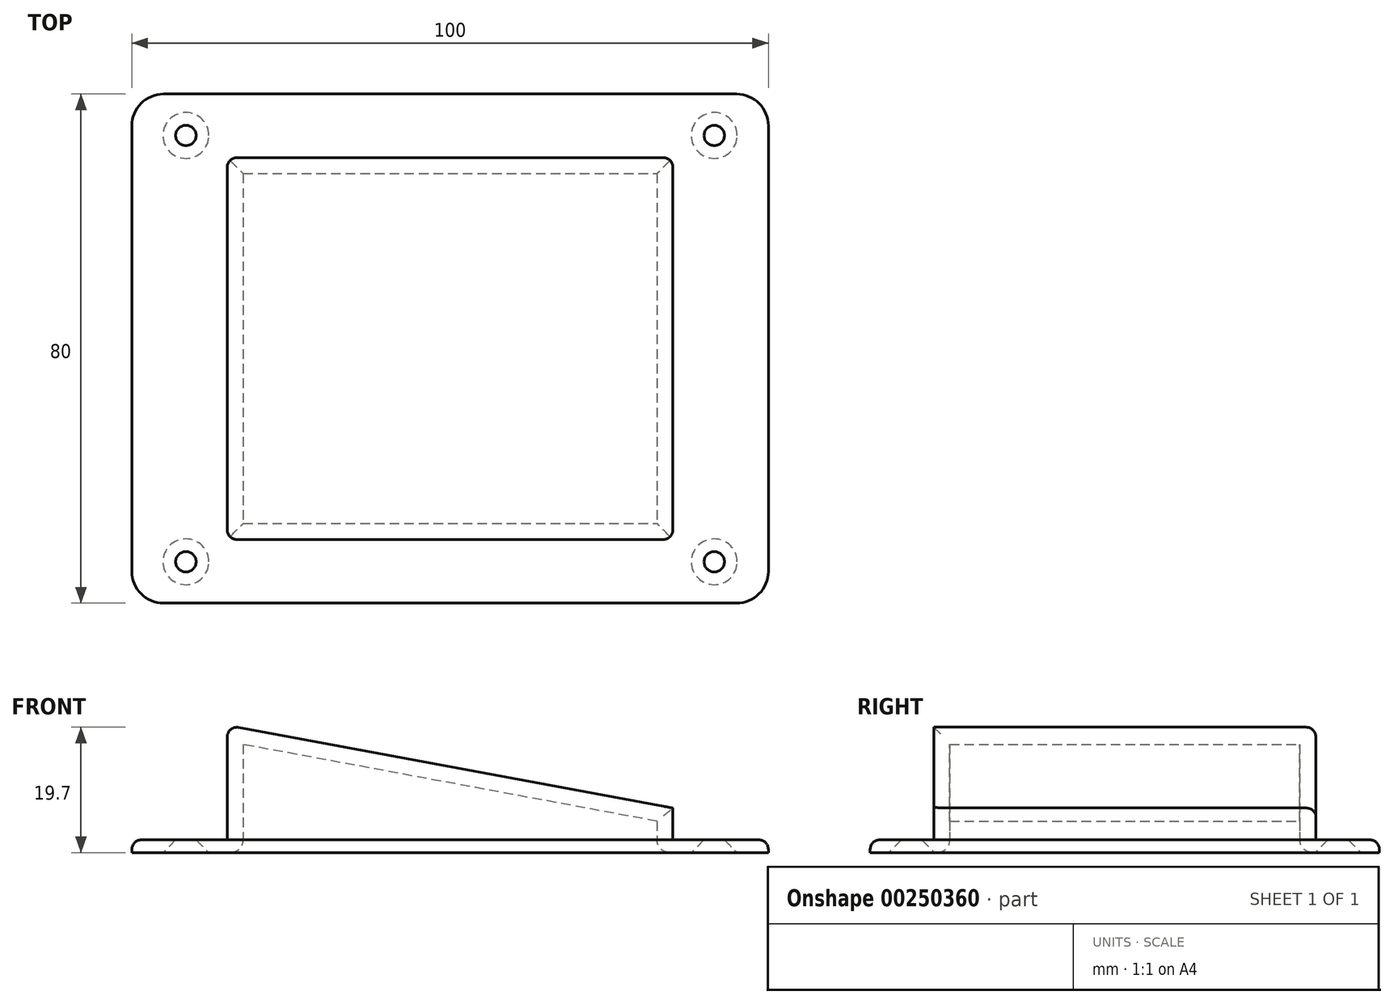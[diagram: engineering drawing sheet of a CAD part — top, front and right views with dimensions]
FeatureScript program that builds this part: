
annotation { "Feature Type Name" : "Feature", "Feature Type Description" : "" }
export const myFeature = defineFeature(function(context is Context, id is Id, definition is map)
    precondition{}
    {
        {
            var Q0;
            Q0=qCreatedBy(makeId("Top.planeOp"),FACE);
            var sketch = newSketch(context, id + "F0", { "sketchPlane" : qUnion([Q0])});
            skLineSegment(sketch, "E0.bottom", {"start": v(50, -40) * mm, "end": v(-50, -40) * mm});
            skLineSegment(sketch, "E0.top", {"start": v(50, 40) * mm, "end": v(-50, 40) * mm});
            skLineSegment(sketch, "E0.left", {"start": v(50, -40) * mm, "end": v(50, 40) * mm});
            skLineSegment(sketch, "E0.right", {"start": v(-50, -40) * mm, "end": v(-50, 40) * mm});
            skPoint(sketch, "E0.middle", {"position": v(0, 0) * mm});
            skSolve(sketch);
        }
        {
            var Q0;
            Q0=qSketchRegion(id+"F0",true);
            extrude(context, id + "F1", {"entities" : qUnion([Q0]), "depth" : 2 * mm});
        }
        {
            var Q0;
            Q0=makeQuery(id+"F1.opExtrude","CAP_FACE",FACE,{"disambiguationData":[OSD([sQuery(id+"F0.wireOp",EDGE,"E0.bottom"),sQuery(id+"F0.wireOp",EDGE,"E0.top"),sQuery(id+"F0.wireOp",EDGE,"E0.left"),sQuery(id+"F0.wireOp",EDGE,"E0.right")])],"isStart":false});
            var sketch = newSketch(context, id + "F2", { "sketchPlane" : qUnion([Q0])});
            skLineSegment(sketch, "E1.bottom", {"start": v(35, -30) * mm, "end": v(-35, -30) * mm});
            skLineSegment(sketch, "E1.top", {"start": v(35, 30) * mm, "end": v(-35, 30) * mm});
            skLineSegment(sketch, "E1.left", {"start": v(35, -30) * mm, "end": v(35, 30) * mm});
            skLineSegment(sketch, "E1.right", {"start": v(-35, -30) * mm, "end": v(-35, 30) * mm});
            skPoint(sketch, "E1.middle", {"position": v(0, 0) * mm});
            skSolve(sketch);
        }
        {
            var Q0;
            Q0=qSketchRegion(id+"F2",true);
            extrude(context, id + "F3", {"entities" : qUnion([Q0]), "operationType" : NewBodyOperationType.ADD, "depth" : 18 * mm});
        }
        {
            var Q0;
            Q0=makeQuery(id+"F3.opExtrude","CAP_FACE",FACE,{"disambiguationData":[OSD([sQuery(id+"F2.wireOp",EDGE,"E1.bottom"),sQuery(id+"F2.wireOp",EDGE,"E1.top"),sQuery(id+"F2.wireOp",EDGE,"E1.left"),sQuery(id+"F2.wireOp",EDGE,"E1.right")])],"isStart":false});
            shell(context, id + "F4", {"entities" : qUnion([Q0]), "thickness" : 2.5 * mm});
        }
        {
            var Q0;
            Q0=makeQuery(id+"F3.opExtrude","SWEPT_FACE",FACE,{"disambiguationData":[OSD([sQuery(id+"F2.wireOp",EDGE,"E1.bottom")])]});
            var sketch = newSketch(context, id + "F5", { "sketchPlane" : qUnion([Q0])});
            skLineSegment(sketch, "E2", {"start": v(-31.99, 7) * mm, "end": v(36.9, 7) * mm});
            skLineSegment(sketch, "E3", {"start": v(-35, 20) * mm, "end": v(35, 7) * mm});
            skLineSegment(sketch, "E4", {"start": v(35, 7) * mm, "end": v(35, 20) * mm});
            skLineSegment(sketch, "E5", {"start": v(35, 20) * mm, "end": v(-35, 20) * mm});
            skSolve(sketch);
        }
        {
            var Q0;
            Q0=qSketchRegion(id+"F5",true);
            extrude(context, id + "F6", {"entities" : qUnion([Q0]), "operationType" : NewBodyOperationType.REMOVE, "oppositeDirection" : true, "depth" : 120 * mm});
        }
        {
            var Q0;
            Q0=makeQuery(id+"F4.opShell","OFFSET_FACE",FACE,{"disambiguationData":[OSD([sQuery(id+"F0.wireOp",EDGE,"E0.bottom"),sQuery(id+"F0.wireOp",EDGE,"E0.top"),sQuery(id+"F0.wireOp",EDGE,"E0.left"),sQuery(id+"F0.wireOp",EDGE,"E0.right")])]});
            extrude(context, id + "F7", {"entities" : qUnion([Q0]), "operationType" : NewBodyOperationType.REMOVE, "oppositeDirection" : true, "depth" : 10 * mm});
        }
        {
            var Q0;
            Q0=makeQuery(id+"F6.boolean.opBoolean","COPY",FACE,{"derivedFrom":makeQuery(id+"F6.opExtrude","SWEPT_FACE",FACE,{"disambiguationData":[OSD([sQuery(id+"F5.wireOp",EDGE,"E3")])]})});
            var sketch = newSketch(context, id + "F8", { "sketchPlane" : qUnion([Q0])});
            skLineSegment(sketch, "E6.bottom", {"start": v(33.13, -30) * mm, "end": v(-37.75, -30) * mm});
            skLineSegment(sketch, "E6.top", {"start": v(33.13, 30) * mm, "end": v(-37.75, 30) * mm});
            skLineSegment(sketch, "E6.left", {"start": v(33.13, -30) * mm, "end": v(33.13, 30) * mm});
            skLineSegment(sketch, "E6.right", {"start": v(-37.75, -30) * mm, "end": v(-37.75, 30) * mm});
            skPoint(sketch, "E6.middle", {"position": v(-2.31, 0) * mm});
            skSolve(sketch);
        }
        {
            var Q0;
            Q0=makeQuery(id+"F8.imprint","IMPRINT",FACE,{"disambiguationData":[TD([[makeQuery(id+"F8.imprint","IMPRINT",EDGE,{"derivedFrom":sQuery(id+"F8.wireOp",EDGE,"E6.bottom")}),1.0]])]});
            var sketch = newSketch(context, id + "F9", { "sketchPlane" : qUnion([Q0])});
            skLineSegment(sketch, "E7.bottom", {"start": v(33.06, -29.96) * mm, "end": v(-38, -29.96) * mm});
            skLineSegment(sketch, "E7.top", {"start": v(33.06, 29.96) * mm, "end": v(-38, 29.96) * mm});
            skLineSegment(sketch, "E7.left", {"start": v(33.06, -29.96) * mm, "end": v(33.06, 29.96) * mm});
            skLineSegment(sketch, "E7.right", {"start": v(-38, -29.96) * mm, "end": v(-38, 29.96) * mm});
            skPoint(sketch, "E7.middle", {"position": v(-2.48, 0) * mm});
            skSolve(sketch);
        }
        {
            var Q0;
            Q0=qSketchRegion(id+"F9",true);
            extrude(context, id + "F10", {"entities" : qUnion([Q0]), "operationType" : NewBodyOperationType.ADD, "oppositeDirection" : true, "depth" : 2.5 * mm});
        }
        {
            var Q0;
            Q0=makeQuery(id+"F10.opExtrude","SWEPT_FACE",FACE,{"disambiguationData":[OSD([sQuery(id+"F9.wireOp",EDGE,"E7.bottom")])]});
            var sketch = newSketch(context, id + "F11", { "sketchPlane" : qUnion([Q0])});
            skLineSegment(sketch, "E8", {"start": v(-35, 19.7) * mm, "end": v(-35.4, 17.53) * mm});
            skLineSegment(sketch, "E9", {"start": v(-35.4, 17.53) * mm, "end": v(-35, 17.46) * mm});
            skLineSegment(sketch, "E10", {"start": v(-35, 17.46) * mm, "end": v(-35, 19.7) * mm});
            skSolve(sketch);
        }
        {
            var Q0;
            Q0=makeQuery(id+"F11.imprint","IMPRINT",FACE,{"disambiguationData":[TD([[makeQuery(id+"F11.imprint","IMPRINT",EDGE,{"derivedFrom":sQuery(id+"F11.wireOp",EDGE,"E8")}),-1.0]])]});
            extrude(context, id + "F12", {"entities" : qUnion([Q0]), "operationType" : NewBodyOperationType.REMOVE, "oppositeDirection" : true, "depth" : 120 * mm});
        }
        {
            var Q0;
            Q0=makeQuery(id+"F6.boolean.opBoolean","COPY",EDGE,{"derivedFrom":makeQuery(id+"F6.opExtrude","CAP_EDGE",EDGE,{"disambiguationData":[OSD([sQuery(id+"F5.wireOp",EDGE,"E3")])],"isStart":true})});
            var Q1;
            {var subQ0=sQuery(id+"F2.wireOp",EDGE,"E1.right");Q1=makeQuery(id+"F6.boolean.opBoolean","MERGE",EDGE,{"derivedFrom":[makeQuery(id+"F3.opExtrude","CAP_EDGE",EDGE,{"disambiguationData":[OSD([subQ0])],"isStart":false}),makeQuery(id+"F6.opExtrude","SWEPT_EDGE",EDGE,{"disambiguationData":[OSD([sQuery(id+"F2.wireOp",EDGE,"E1.bottom"),subQ0,sQuery(id+"F5.wireOp",EDGE,"E3"),sQuery(id+"F5.wireOp",EDGE,"E5")])]})]});}
            var Q2;
            Q2=makeQuery(id+"F3.opExtrude","SWEPT_EDGE",EDGE,{"disambiguationData":[OSD([sQuery(id+"F2.wireOp",EDGE,"E1.bottom"),sQuery(id+"F2.wireOp",EDGE,"E1.right")])]});
            var Q3;
            Q3=makeQuery(id+"F6.boolean.opBoolean","COPY",EDGE,{"derivedFrom":makeQuery(id+"F6.opExtrude","SWEPT_EDGE",EDGE,{"disambiguationData":[OSD([sQuery(id+"F2.wireOp",EDGE,"E1.bottom"),sQuery(id+"F2.wireOp",EDGE,"E1.left"),sQuery(id+"F5.wireOp",EDGE,"E3"),sQuery(id+"F5.wireOp",EDGE,"E4")])]})});
            var Q4;
            Q4=makeQuery(id+"F3.opExtrude","SWEPT_EDGE",EDGE,{"disambiguationData":[OSD([sQuery(id+"F2.wireOp",EDGE,"E1.bottom"),sQuery(id+"F2.wireOp",EDGE,"E1.left")])]});
            var Q5;
            Q5=makeQuery(id+"F1.opExtrude","CAP_EDGE",EDGE,{"disambiguationData":[OSD([sQuery(id+"F0.wireOp",EDGE,"E0.bottom")])],"isStart":false});
            var Q6;
            Q6=makeQuery(id+"F1.opExtrude","CAP_EDGE",EDGE,{"disambiguationData":[OSD([sQuery(id+"F0.wireOp",EDGE,"E0.left")])],"isStart":false});
            var Q7;
            Q7=makeQuery(id+"F1.opExtrude","CAP_EDGE",EDGE,{"disambiguationData":[OSD([sQuery(id+"F0.wireOp",EDGE,"E0.top")])],"isStart":false});
            var Q8;
            Q8=makeQuery(id+"F3.opExtrude","SWEPT_EDGE",EDGE,{"disambiguationData":[OSD([sQuery(id+"F2.wireOp",EDGE,"E1.top"),sQuery(id+"F2.wireOp",EDGE,"E1.left")])]});
            var Q9;
            Q9=makeQuery(id+"F3.opExtrude","SWEPT_EDGE",EDGE,{"disambiguationData":[OSD([sQuery(id+"F2.wireOp",EDGE,"E1.top"),sQuery(id+"F2.wireOp",EDGE,"E1.right")])]});
            var Q10;
            Q10=makeQuery(id+"F6.boolean.opBoolean","INTERSECT",EDGE,{"derivedFrom":[makeQuery(id+"F3.opExtrude","SWEPT_FACE",FACE,{"disambiguationData":[OSD([sQuery(id+"F2.wireOp",EDGE,"E1.top")])]}),makeQuery(id+"F6.opExtrude","SWEPT_FACE",FACE,{"disambiguationData":[OSD([sQuery(id+"F5.wireOp",EDGE,"E3")])]})]});
            var Q11;
            Q11=makeQuery(id+"F1.opExtrude","CAP_EDGE",EDGE,{"disambiguationData":[OSD([sQuery(id+"F0.wireOp",EDGE,"E0.right")])],"isStart":false});
            fillet(context, id + "F13", {"entities" : qUnion([Q0, Q1, Q2, Q3, Q4, Q5, Q6, Q7, Q8, Q9, Q10, Q11]), "radius" : 1.5 * mm, "tangentPropagation" : true, "allowEdgeOverflow" : false});
        }
        {
            var Q0;
            Q0=makeQuery(id+"F2.imprint","IMPRINT",FACE,{"disambiguationData":[TD([[makeQuery(id+"F2.imprint","IMPRINT",EDGE,{"derivedFrom":sQuery(id+"F2.wireOp",EDGE,"E1.bottom")}),1.0]])]});
            var sketch = newSketch(context, id + "F14", { "sketchPlane" : qUnion([Q0])});
            skLineSegment(sketch, "E11", {"start": v(-41.5, 39.73) * mm, "end": v(-41.5, -39.02) * mm, "construction": true});
            skLineSegment(sketch, "E12", {"start": v(-50.33, 33.5) * mm, "end": v(50.2, 33.5) * mm, "construction": true});
            skLineSegment(sketch, "E13.MirrorCS", {"start": v(-50.33, -33.5) * mm, "end": v(50.2, -33.5) * mm, "construction": true});
            skLineSegment(sketch, "E14.MirrorCS", {"start": v(41.5, 39.73) * mm, "end": v(41.5, -39.02) * mm, "construction": true});
            skCircle(sketch, "E15", {"center": v(-41.5, 33.5) * mm, "radius": 1.6 * mm});
            skCircle(sketch, "E16.MirrorC", {"center": v(41.5, 33.5) * mm, "radius": 1.6 * mm});
            skCircle(sketch, "E17.MirrorC", {"center": v(-41.5, -33.5) * mm, "radius": 1.6 * mm});
            skCircle(sketch, "E18.MirrorC", {"center": v(41.5, -33.5) * mm, "radius": 1.6 * mm});
            skSolve(sketch);
        }
        {
            var Q0;
            Q0 = qSketchRegion(id + "F14", true);
            extrude(context, id + "F15", {"entities" : qUnion([Q0]), "operationType" : NewBodyOperationType.REMOVE, "oppositeDirection" : true, "depth" : 10 * mm});
        }
        {
            var Q0;
            Q0=makeQuery(id+"F13.opFillet","BLEND_EDGE",EDGE,{"blendedFrom":[makeQuery(id+"F1.opExtrude","CAP_EDGE",EDGE,{"disambiguationData":[OSD([sQuery(id+"F0.wireOp",EDGE,"E0.top")])],"isStart":false}),makeQuery(id+"F1.opExtrude","CAP_EDGE",EDGE,{"disambiguationData":[OSD([sQuery(id+"F0.wireOp",EDGE,"E0.left")])],"isStart":false})],"blendedInto":[]});
            var Q1;
            Q1=makeQuery(id+"F13.opFillet","BLEND_EDGE",EDGE,{"blendedFrom":[makeQuery(id+"F1.opExtrude","CAP_EDGE",EDGE,{"disambiguationData":[OSD([sQuery(id+"F0.wireOp",EDGE,"E0.top")])],"isStart":false}),makeQuery(id+"F1.opExtrude","CAP_EDGE",EDGE,{"disambiguationData":[OSD([sQuery(id+"F0.wireOp",EDGE,"E0.right")])],"isStart":false})],"blendedInto":[]});
            var Q2;
            Q2=makeQuery(id+"F13.opFillet","BLEND_EDGE",EDGE,{"blendedFrom":[makeQuery(id+"F1.opExtrude","CAP_EDGE",EDGE,{"disambiguationData":[OSD([sQuery(id+"F0.wireOp",EDGE,"E0.bottom")])],"isStart":false}),makeQuery(id+"F1.opExtrude","CAP_EDGE",EDGE,{"disambiguationData":[OSD([sQuery(id+"F0.wireOp",EDGE,"E0.right")])],"isStart":false})],"blendedInto":[]});
            var Q3;
            Q3=makeQuery(id+"F13.opFillet","BLEND_EDGE",EDGE,{"blendedFrom":[makeQuery(id+"F1.opExtrude","CAP_EDGE",EDGE,{"disambiguationData":[OSD([sQuery(id+"F0.wireOp",EDGE,"E0.bottom")])],"isStart":false}),makeQuery(id+"F1.opExtrude","CAP_EDGE",EDGE,{"disambiguationData":[OSD([sQuery(id+"F0.wireOp",EDGE,"E0.left")])],"isStart":false})],"blendedInto":[]});
            fillet(context, id + "F16", {"entities" : qUnion([Q0, Q1, Q2, Q3]), "radius" : 5 * mm, "tangentPropagation" : true, "allowEdgeOverflow" : false});
        }
        {
            var Q0;
            Q0=makeQuery(id+"F15.boolean.opBoolean","INTERSECT",EDGE,{"derivedFrom":[makeQuery(id+"F1.opExtrude","CAP_FACE",FACE,{"disambiguationData":[OSD([sQuery(id+"F0.wireOp",EDGE,"E0.bottom"),sQuery(id+"F0.wireOp",EDGE,"E0.top"),sQuery(id+"F0.wireOp",EDGE,"E0.left"),sQuery(id+"F0.wireOp",EDGE,"E0.right")])],"isStart":true}),makeQuery(id+"F15.opExtrude","SWEPT_FACE",FACE,{"disambiguationData":[OSD([sQuery(id+"F14.wireOp",EDGE,"E18.MirrorC")])]})]});
            var Q1;
            Q1=makeQuery(id+"F15.boolean.opBoolean","INTERSECT",EDGE,{"derivedFrom":[makeQuery(id+"F1.opExtrude","CAP_FACE",FACE,{"disambiguationData":[OSD([sQuery(id+"F0.wireOp",EDGE,"E0.bottom"),sQuery(id+"F0.wireOp",EDGE,"E0.top"),sQuery(id+"F0.wireOp",EDGE,"E0.left"),sQuery(id+"F0.wireOp",EDGE,"E0.right")])],"isStart":true}),makeQuery(id+"F15.opExtrude","SWEPT_FACE",FACE,{"disambiguationData":[OSD([sQuery(id+"F14.wireOp",EDGE,"E16.MirrorC")])]})]});
            var Q2;
            Q2=makeQuery(id+"F15.boolean.opBoolean","INTERSECT",EDGE,{"derivedFrom":[makeQuery(id+"F1.opExtrude","CAP_FACE",FACE,{"disambiguationData":[OSD([sQuery(id+"F0.wireOp",EDGE,"E0.bottom"),sQuery(id+"F0.wireOp",EDGE,"E0.top"),sQuery(id+"F0.wireOp",EDGE,"E0.left"),sQuery(id+"F0.wireOp",EDGE,"E0.right")])],"isStart":true}),makeQuery(id+"F15.opExtrude","SWEPT_FACE",FACE,{"disambiguationData":[OSD([sQuery(id+"F14.wireOp",EDGE,"E17.MirrorC")])]})]});
            var Q3;
            Q3=makeQuery(id+"F15.boolean.opBoolean","INTERSECT",EDGE,{"derivedFrom":[makeQuery(id+"F1.opExtrude","CAP_FACE",FACE,{"disambiguationData":[OSD([sQuery(id+"F0.wireOp",EDGE,"E0.bottom"),sQuery(id+"F0.wireOp",EDGE,"E0.top"),sQuery(id+"F0.wireOp",EDGE,"E0.left"),sQuery(id+"F0.wireOp",EDGE,"E0.right")])],"isStart":true}),makeQuery(id+"F15.opExtrude","SWEPT_FACE",FACE,{"disambiguationData":[OSD([sQuery(id+"F14.wireOp",EDGE,"E15")])]})]});
            chamfer(context, id + "F17", {"entities" : qUnion([Q0, Q1, Q2, Q3]), "width" : 2 * mm, "tangentPropagation" : true});
        }
        {
            var Q0;
            {var subQ0=sQuery(id+"F0.wireOp",EDGE,"E0.right");var subQ1=sQuery(id+"F0.wireOp",EDGE,"E0.left");var subQ2=sQuery(id+"F0.wireOp",EDGE,"E0.top");var subQ3=sQuery(id+"F0.wireOp",EDGE,"E0.bottom");Q0=makeQuery(id+"F7.boolean.opBoolean","INTERSECT",EDGE,{"derivedFrom":[makeQuery(id+"F1.opExtrude","CAP_FACE",FACE,{"disambiguationData":[OSD([subQ3,subQ2,subQ1,subQ0])],"isStart":true}),makeQuery(id+"F7.opExtrude","SWEPT_FACE",FACE,{"disambiguationData":[OSD([subQ3,subQ2,subQ1,subQ0,sQuery(id+"F2.wireOp",EDGE,"E1.left")])]})]});}
            var Q1;
            {var subQ0=sQuery(id+"F0.wireOp",EDGE,"E0.right");var subQ1=sQuery(id+"F0.wireOp",EDGE,"E0.left");var subQ2=sQuery(id+"F0.wireOp",EDGE,"E0.top");var subQ3=sQuery(id+"F0.wireOp",EDGE,"E0.bottom");Q1=makeQuery(id+"F7.boolean.opBoolean","INTERSECT",EDGE,{"derivedFrom":[makeQuery(id+"F1.opExtrude","CAP_FACE",FACE,{"disambiguationData":[OSD([subQ3,subQ2,subQ1,subQ0])],"isStart":true}),makeQuery(id+"F7.opExtrude","SWEPT_FACE",FACE,{"disambiguationData":[OSD([subQ3,subQ2,subQ1,subQ0,sQuery(id+"F2.wireOp",EDGE,"E1.bottom")])]})]});}
            var Q2;
            {var subQ0=sQuery(id+"F0.wireOp",EDGE,"E0.right");var subQ1=sQuery(id+"F0.wireOp",EDGE,"E0.left");var subQ2=sQuery(id+"F0.wireOp",EDGE,"E0.top");var subQ3=sQuery(id+"F0.wireOp",EDGE,"E0.bottom");Q2=makeQuery(id+"F7.boolean.opBoolean","INTERSECT",EDGE,{"derivedFrom":[makeQuery(id+"F1.opExtrude","CAP_FACE",FACE,{"disambiguationData":[OSD([subQ3,subQ2,subQ1,subQ0])],"isStart":true}),makeQuery(id+"F7.opExtrude","SWEPT_FACE",FACE,{"disambiguationData":[OSD([subQ3,subQ2,subQ1,subQ0,sQuery(id+"F2.wireOp",EDGE,"E1.top")])]})]});}
            var Q3;
            {var subQ0=sQuery(id+"F0.wireOp",EDGE,"E0.right");var subQ1=sQuery(id+"F0.wireOp",EDGE,"E0.left");var subQ2=sQuery(id+"F0.wireOp",EDGE,"E0.top");var subQ3=sQuery(id+"F0.wireOp",EDGE,"E0.bottom");Q3=makeQuery(id+"F7.boolean.opBoolean","INTERSECT",EDGE,{"derivedFrom":[makeQuery(id+"F1.opExtrude","CAP_FACE",FACE,{"disambiguationData":[OSD([subQ3,subQ2,subQ1,subQ0])],"isStart":true}),makeQuery(id+"F7.opExtrude","SWEPT_FACE",FACE,{"disambiguationData":[OSD([subQ3,subQ2,subQ1,subQ0,sQuery(id+"F2.wireOp",EDGE,"E1.right")])]})]});}
            fillet(context, id + "F18", {"entities" : qUnion([Q0, Q1, Q2, Q3]), "radius" : 2 * mm, "tangentPropagation" : true, "allowEdgeOverflow" : false});
        }
    });
